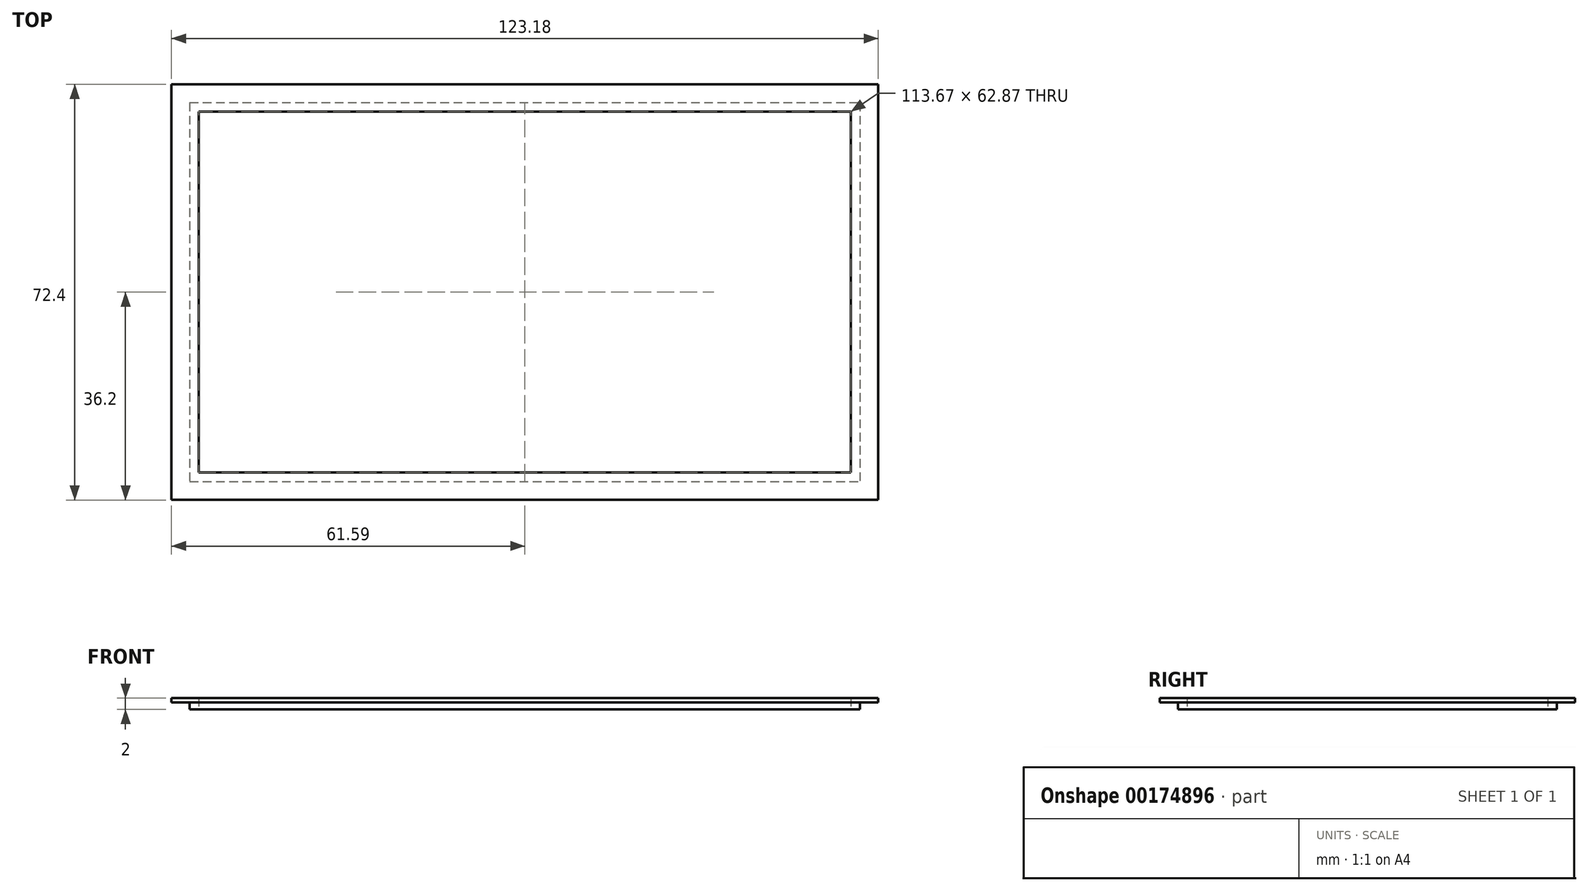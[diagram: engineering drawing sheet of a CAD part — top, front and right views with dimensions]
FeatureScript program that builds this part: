
annotation { "Feature Type Name" : "Feature", "Feature Type Description" : "" }
export const myFeature = defineFeature(function(context is Context, id is Id, definition is map)
    precondition{}
    {
        {
            var Q0;
            Q0=qCreatedBy(makeId("Top.planeOp"),FACE);
            var sketch = newSketch(context, id + "F0", { "sketchPlane" : qUnion([Q0])});
            skLineSegment(sketch, "E0.bottom", {"start": v(-58.42, 33.02) * mm, "end": v(58.42, 33.02) * mm});
            skLineSegment(sketch, "E0.top", {"start": v(-58.42, -33.02) * mm, "end": v(58.42, -33.02) * mm});
            skLineSegment(sketch, "E0.left", {"start": v(-58.42, 33.02) * mm, "end": v(-58.42, -33.02) * mm});
            skLineSegment(sketch, "E0.right", {"start": v(58.42, 33.02) * mm, "end": v(58.42, -33.02) * mm});
            skPoint(sketch, "E0.middle", {"position": v(0, 0) * mm});
            skLineSegment(sketch, "E1.0", {"start": v(-56.83, 31.43) * mm, "end": v(56.83, 31.43) * mm});
            skLineSegment(sketch, "E1.1", {"start": v(-56.83, 31.43) * mm, "end": v(-56.83, -31.43) * mm});
            skLineSegment(sketch, "E1.2", {"start": v(-56.83, -31.43) * mm, "end": v(56.83, -31.43) * mm});
            skLineSegment(sketch, "E1.3", {"start": v(56.83, 31.43) * mm, "end": v(56.83, -31.43) * mm});
            skLineSegment(sketch, "E2.0", {"start": v(-61.6, 36.2) * mm, "end": v(-61.6, -36.2) * mm});
            skLineSegment(sketch, "E2.1", {"start": v(-61.6, 36.2) * mm, "end": v(61.6, 36.2) * mm});
            skLineSegment(sketch, "E2.2", {"start": v(61.6, 36.2) * mm, "end": v(61.6, -36.2) * mm});
            skLineSegment(sketch, "E2.3", {"start": v(-61.6, -36.2) * mm, "end": v(61.6, -36.2) * mm});
            skSolve(sketch);
        }
        {
            var Q0;
            Q0 = qSketchRegion(id + "F0", true);
            var Q1;
            Q1=makeQuery(id+"F0.imprint","IMPRINT",FACE,{"disambiguationData":[TD([[makeQuery(id+"F0.imprint","IMPRINT",EDGE,{"derivedFrom":sQuery(id+"F0.wireOp",EDGE,"E0.bottom")}),-1.0]])]});
            extrude(context, id + "F1", {"entities" : qUnion([Q0, Q1]), "depth" : .75 * mm});
        }
        {
            var Q0;
            Q0=makeQuery(id+"F0.imprint","IMPRINT",FACE,{"disambiguationData":[TD([[makeQuery(id+"F0.imprint","IMPRINT",EDGE,{"derivedFrom":sQuery(id+"F0.wireOp",EDGE,"E0.bottom")}),-1.0]])]});
            extrude(context, id + "F2", {"entities" : qUnion([Q0]), "operationType" : NewBodyOperationType.ADD, "oppositeDirection" : true, "depth" : 1.25 * mm});
        }
    });
